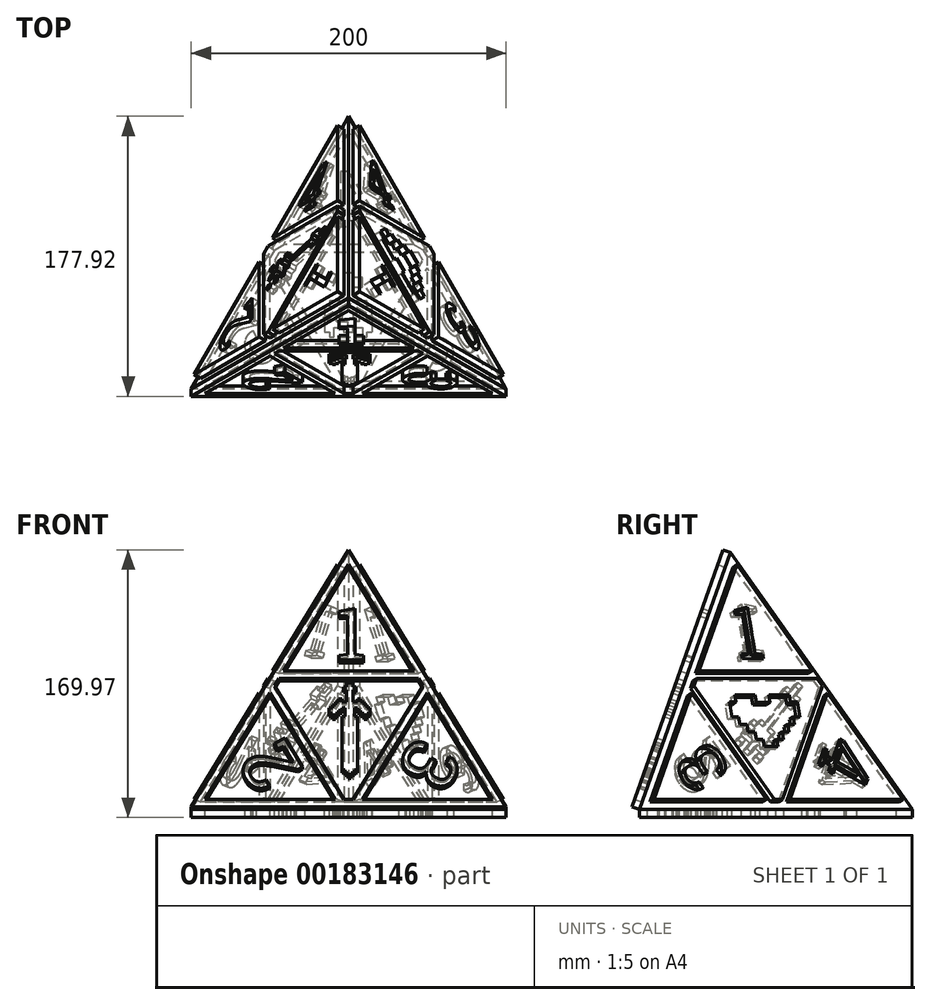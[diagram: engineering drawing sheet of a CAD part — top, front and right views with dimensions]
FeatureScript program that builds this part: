
annotation { "Feature Type Name" : "Feature", "Feature Type Description" : "" }
export const myFeature = defineFeature(function(context is Context, id is Id, definition is map)
    precondition{}
    {
        {
            var Q0;
            Q0=qCreatedBy(makeId("Top.planeOp"),FACE);
            var sketch = newSketch(context, id + "F0", { "sketchPlane" : qUnion([Q0])});
            skLineSegment(sketch, "E0", {"start": v(0, 115.47) * mm, "end": v(100, -57.74) * mm});
            skLineSegment(sketch, "E1", {"start": v(100, -57.74) * mm, "end": v(-100, -57.74) * mm});
            skLineSegment(sketch, "E2", {"start": v(-100, -57.74) * mm, "end": v(0, 115.47) * mm});
            skLineSegment(sketch, "E3", {"start": v(0, 115.47) * mm, "end": v(0, 0) * mm});
            skLineSegment(sketch, "E4", {"start": v(-100, -57.74) * mm, "end": v(0, 0) * mm});
            skLineSegment(sketch, "E5", {"start": v(0, 0) * mm, "end": v(100, -57.74) * mm});
            skPoint(sketch, "E6.orphan", {"position": v(0, -57.74) * mm});
            skLineSegment(sketch, "E7", {"start": v(0, 115.47) * mm, "end": v(0, -57.74) * mm, "construction": true});
            skSolve(sketch);
        }
        {
            assignVariable(context, id + "F1", {"name" : "Angle", "anyValue" : 70.53});
        }
        {
            var Q0;
            Q0=qSketchRegion(id+"F0",true);
            extrude(context, id + "F2", {"entities" : qUnion([Q0]), "depth" : 1000 * mm, "hasDraft" : true, "draftAngle" : (90 - getVariable(context, 'Angle')) * degree, "draftPullDirection" : true});
        }
        {
            var Q0;
            Q0=makeQuery(id+"F2.opExtrude","SWEPT_FACE",FACE,{"disambiguationData":[OSD([sQuery(id+"F0.wireOp",EDGE,"E1")])]});
            var sketch = newSketch(context, id + "F3", { "sketchPlane" : qUnion([Q0])});
            skLineSegment(sketch, "E8", {"start": v(0, 153.96) * mm, "end": v(-100, -19.24) * mm});
            skLineSegment(sketch, "E9", {"start": v(-100, -19.24) * mm, "end": v(100, -19.24) * mm});
            skLineSegment(sketch, "E10", {"start": v(100, -19.24) * mm, "end": v(0, 153.96) * mm});
            skLineSegment(sketch, "E11", {"start": v(-2.89, -14.24) * mm, "end": v(-47.11, 62.36) * mm});
            skLineSegment(sketch, "E12", {"start": v(-44.23, 67.36) * mm, "end": v(44.23, 67.36) * mm});
            skLineSegment(sketch, "E13", {"start": v(47.11, 62.36) * mm, "end": v(2.89, -14.24) * mm});
            skLineSegment(sketch, "E14.0", {"start": v(91.34, -14.24) * mm, "end": v(50, 57.36) * mm});
            skLineSegment(sketch, "E15.0", {"start": v(-41.34, 72.36) * mm, "end": v(41.34, 72.36) * mm});
            skLineSegment(sketch, "E16.0", {"start": v(50, 57.36) * mm, "end": v(8.66, -14.24) * mm});
            skLineSegment(sketch, "E17.trimOffspring", {"start": v(-44.23, 67.36) * mm, "end": v(-47.11, 62.36) * mm});
            skPoint(sketch, "E18.orphan", {"position": v(-50, 67.36) * mm});
            skLineSegment(sketch, "E19.trimOffspring", {"start": v(-50, 57.36) * mm, "end": v(-91.34, -14.24) * mm});
            skLineSegment(sketch, "E20.trimOffspring", {"start": v(41.34, 72.36) * mm, "end": v(0, 143.96) * mm});
            skPoint(sketch, "E21.orphan", {"position": v(50, 67.36) * mm});
            skLineSegment(sketch, "E22.trimOffspring", {"start": v(47.11, 62.36) * mm, "end": v(44.23, 67.36) * mm});
            skLineSegment(sketch, "E23.trimOffspring", {"start": v(-8.66, -14.24) * mm, "end": v(-50, 57.36) * mm});
            skLineSegment(sketch, "E24.trimOffspring", {"start": v(-2.89, -14.24) * mm, "end": v(2.89, -14.24) * mm});
            skLineSegment(sketch, "E25.trimOffspring", {"start": v(8.66, -14.24) * mm, "end": v(91.34, -14.24) * mm});
            skPoint(sketch, "E26.orphan", {"position": v(0, -19.24) * mm});
            skLineSegment(sketch, "E27.trimOffspring", {"start": v(-91.34, -14.24) * mm, "end": v(-8.66, -14.24) * mm});
            skLineSegment(sketch, "E28.trimOffspring", {"start": v(0, 143.96) * mm, "end": v(-41.34, 72.36) * mm});
            skSolve(sketch);
        }
        {
            var Q0;
            Q0=makeQuery(id+"F3.imprint","IMPRINT",FACE,{"disambiguationData":[TD([[makeQuery(id+"F3.imprint","IMPRINT",EDGE,{"derivedFrom":sQuery(id+"F3.wireOp",EDGE,"E8")}),1.0]])]});
            extrude(context, id + "F4", {"entities" : qUnion([Q0]), "operationType" : NewBodyOperationType.ADD, "depth" : 5 * mm});
        }
        {
            var Q0;
            Q0=makeQuery(id+"F4.boolean.opBoolean","SPLIT",FACE,{"disambiguationData":[TD([makeQuery(id+"F4.opExtrude","SWEPT_FACE",FACE,{"disambiguationData":[OSD([sQuery(id+"F3.wireOp",EDGE,"E15.0")])]})])],"derivedFrom":makeQuery(id+"F2.opExtrude","SWEPT_FACE",FACE,{"disambiguationData":[OSD([sQuery(id+"F0.wireOp",EDGE,"E1")])]})});
            var sketch = newSketch(context, id + "F5", { "sketchPlane" : qUnion([Q0])});
            skText(sketch, "E29", { "text": "1", "fontName": "RobotoSlab-Regular.ttf"});
            const initialGuessF5  = {"E29": [-0.00906, 0.07964, 1, 0, 0.03527]};
            skSetInitialGuess(sketch, initialGuessF5);
            skSolve(sketch);
        }
        {
            var Q0;
            Q0=makeQuery(id+"F5.imprint","IMPRINT",FACE,{"disambiguationData":[TD([[makeQuery(id+"F5.imprint","IMPRINT",EDGE,{"derivedFrom":sQuery(id+"F5.wireOp",EDGE,"E29.sketch_text.stroke-0")}),-1.0]])]});
            extrude(context, id + "F6", {"entities" : qUnion([Q0]), "operationType" : NewBodyOperationType.ADD, "depth" : 5 * mm, "hasSecondDirection" : true, "secondDirectionOppositeDirection" : true, "secondDirectionDepth" : 25 * mm});
        }
        {
            var Q0;
            Q0=makeQuery(id+"F4.boolean.opBoolean","SPLIT",FACE,{"disambiguationData":[TD([makeQuery(id+"F4.opExtrude","SWEPT_FACE",FACE,{"disambiguationData":[OSD([sQuery(id+"F3.wireOp",EDGE,"E19.trimOffspring")])]})])],"derivedFrom":makeQuery(id+"F2.opExtrude","SWEPT_FACE",FACE,{"disambiguationData":[OSD([sQuery(id+"F0.wireOp",EDGE,"E1")])]})});
            var sketch = newSketch(context, id + "F7", { "sketchPlane" : qUnion([Q0])});
            skText(sketch, "E30", { "text": "2", "fontName": "RobotoSlab-Regular.ttf"});
            const initialGuessF7  = {"E30": [-0.02807, 0.0057, -0.5, 0.86603, 0.03527]};
            skSetInitialGuess(sketch, initialGuessF7);
            skSolve(sketch);
        }
        {
            var Q0;
            Q0=makeQuery(id+"F7.imprint","IMPRINT",FACE,{"disambiguationData":[TD([[makeQuery(id+"F7.imprint","IMPRINT",EDGE,{"derivedFrom":sQuery(id+"F7.wireOp",EDGE,"E30.sketch_text.stroke-0")}),-1.0]])]});
            extrude(context, id + "F8", {"entities" : qUnion([Q0]), "operationType" : NewBodyOperationType.ADD, "depth" : 5 * mm});
        }
        {
            var Q0;
            Q0=makeQuery(id+"F4.boolean.opBoolean","SPLIT",FACE,{"disambiguationData":[TD([makeQuery(id+"F4.opExtrude","SWEPT_FACE",FACE,{"disambiguationData":[OSD([sQuery(id+"F3.wireOp",EDGE,"E14.0")])]})])],"derivedFrom":makeQuery(id+"F2.opExtrude","SWEPT_FACE",FACE,{"disambiguationData":[OSD([sQuery(id+"F0.wireOp",EDGE,"E1")])]})});
            var sketch = newSketch(context, id + "F9", { "sketchPlane" : qUnion([Q0])});
            skText(sketch, "E31", { "text": "3", "fontName": "RobotoSlab-Regular.ttf"});
            const initialGuessF9  = {"E31": [0.04286, 0.02914, -0.5, -0.86603, 0.03527]};
            skSetInitialGuess(sketch, initialGuessF9);
            skSolve(sketch);
        }
        {
            var Q0;
            Q0=makeQuery(id+"F9.imprint","IMPRINT",FACE,{"disambiguationData":[TD([[makeQuery(id+"F9.imprint","IMPRINT",EDGE,{"derivedFrom":sQuery(id+"F9.wireOp",EDGE,"E31.sketch_text.stroke-0")}),-1.0]])]});
            extrude(context, id + "F10", {"entities" : qUnion([Q0]), "operationType" : NewBodyOperationType.ADD, "depth" : 5 * mm});
        }
        {
            var Q0;
            Q0=makeQuery(id+"F2.opExtrude","SWEPT_FACE",FACE,{"disambiguationData":[OSD([sQuery(id+"F0.wireOp",EDGE,"E0")])]});
            var sketch = newSketch(context, id + "F11", { "sketchPlane" : qUnion([Q0])});
            skLineSegment(sketch, "E32", {"start": v(-29.1, 151.19) * mm, "end": v(101.83, 0) * mm});
            skLineSegment(sketch, "E33", {"start": v(101.83, 0) * mm, "end": v(-94.56, -37.8) * mm});
            skLineSegment(sketch, "E34", {"start": v(-92.67, -32.34) * mm, "end": v(-63.72, 51.24) * mm});
            skLineSegment(sketch, "E35", {"start": v(5.53, -13.44) * mm, "end": v(34.48, 70.14) * mm});
            skLineSegment(sketch, "E36", {"start": v(30.7, 74.5) * mm, "end": v(-56.16, 57.79) * mm});
            skLineSegment(sketch, "E37", {"start": v(-58.05, 52.33) * mm, "end": v(-0.14, -14.53) * mm});
            skLineSegment(sketch, "E38.trimOffspring", {"start": v(-27.2, 141.37) * mm, "end": v(26.92, 78.87) * mm});
            skLineSegment(sketch, "E39.trimOffspring", {"start": v(26.92, 78.87) * mm, "end": v(-54.27, 63.24) * mm});
            skPoint(sketch, "E40.orphan", {"position": v(36.37, 75.6) * mm});
            skLineSegment(sketch, "E41.trimOffspring", {"start": v(92.39, 3.27) * mm, "end": v(11.2, -12.35) * mm});
            skPoint(sketch, "E42.orphan", {"position": v(3.64, -18.9) * mm});
            skLineSegment(sketch, "E43.trimOffspring", {"start": v(11.2, -12.35) * mm, "end": v(38.26, 65.77) * mm});
            skLineSegment(sketch, "E44.trimOffspring", {"start": v(-87, -31.25) * mm, "end": v(-59.94, 46.88) * mm});
            skLineSegment(sketch, "E45.trimOffspring", {"start": v(-92.67, -32.34) * mm, "end": v(-95.5, -32.89) * mm});
            skLineSegment(sketch, "E46.trimOffspring", {"start": v(-59.94, 46.88) * mm, "end": v(-5.81, -15.62) * mm});
            skLineSegment(sketch, "E47.trimOffspring", {"start": v(-61.83, 56.7) * mm, "end": v(-29.1, 151.19) * mm});
            skLineSegment(sketch, "E48.trimOffspring", {"start": v(-58.05, 52.33) * mm, "end": v(-56.16, 57.79) * mm});
            skLineSegment(sketch, "E49.trimOffspring", {"start": v(-54.27, 63.24) * mm, "end": v(-27.2, 141.37) * mm});
            skLineSegment(sketch, "E50.trimOffspring", {"start": v(38.26, 65.77) * mm, "end": v(92.39, 3.27) * mm});
            skLineSegment(sketch, "E51.trimOffspring", {"start": v(30.7, 74.5) * mm, "end": v(34.48, 70.14) * mm});
            skLineSegment(sketch, "E52.trimOffspring", {"start": v(-5.81, -15.62) * mm, "end": v(-87, -31.25) * mm});
            skLineSegment(sketch, "E53.trimOffspring", {"start": v(5.53, -13.44) * mm, "end": v(-0.14, -14.53) * mm});
            skLineSegment(sketch, "E54", {"start": v(-63.72, 51.24) * mm, "end": v(-61.83, 56.7) * mm});
            skSolve(sketch);
        }
        {
            var Q0;
            Q0 = qSketchRegion(id + "F11", true);
            extrude(context, id + "F12", {"entities" : qUnion([Q0]), "operationType" : NewBodyOperationType.ADD, "depth" : 5 * mm});
        }
        {
            var Q0;
            Q0=makeQuery(id+"F2.opExtrude","SWEPT_FACE",FACE,{"disambiguationData":[OSD([sQuery(id+"F0.wireOp",EDGE,"E2")])]});
            var sketch = newSketch(context, id + "F13", { "sketchPlane" : qUnion([Q0])});
            skLineSegment(sketch, "E55", {"start": v(29.1, 151.19) * mm, "end": v(-101.83, 0) * mm});
            skLineSegment(sketch, "E56", {"start": v(-101.83, 0) * mm, "end": v(94.56, -37.8) * mm});
            skLineSegment(sketch, "E57", {"start": v(94.56, -37.8) * mm, "end": v(29.1, 151.19) * mm});
            skLineSegment(sketch, "E58", {"start": v(-5.53, -13.44) * mm, "end": v(-34.48, 70.14) * mm});
            skLineSegment(sketch, "E59", {"start": v(-30.7, 74.5) * mm, "end": v(56.16, 57.79) * mm});
            skLineSegment(sketch, "E60", {"start": v(58.05, 52.33) * mm, "end": v(0.14, -14.53) * mm});
            skLineSegment(sketch, "E61.0", {"start": v(27.2, 141.37) * mm, "end": v(-26.92, 78.87) * mm});
            skLineSegment(sketch, "E62.0", {"start": v(-92.39, 3.27) * mm, "end": v(-11.2, -12.35) * mm});
            skLineSegment(sketch, "E63.0", {"start": v(-26.92, 78.87) * mm, "end": v(54.27, 63.24) * mm});
            skLineSegment(sketch, "E64.trimOffspring", {"start": v(54.27, 63.24) * mm, "end": v(27.2, 141.37) * mm});
            skPoint(sketch, "E65.orphan", {"position": v(61.83, 56.7) * mm});
            skLineSegment(sketch, "E66.trimOffspring", {"start": v(58.05, 52.33) * mm, "end": v(56.16, 57.79) * mm});
            skLineSegment(sketch, "E67.trimOffspring", {"start": v(59.94, 46.88) * mm, "end": v(5.81, -15.62) * mm});
            skLineSegment(sketch, "E68.trimOffspring", {"start": v(87, -31.25) * mm, "end": v(59.94, 46.88) * mm});
            skLineSegment(sketch, "E69.trimOffspring", {"start": v(-11.2, -12.35) * mm, "end": v(-38.26, 65.77) * mm});
            skPoint(sketch, "E70.orphan", {"position": v(-3.64, -18.9) * mm});
            skLineSegment(sketch, "E71.trimOffspring", {"start": v(-5.53, -13.44) * mm, "end": v(0.14, -14.53) * mm});
            skLineSegment(sketch, "E72.trimOffspring", {"start": v(5.81, -15.62) * mm, "end": v(87, -31.25) * mm});
            skLineSegment(sketch, "E73.trimOffspring", {"start": v(-38.26, 65.77) * mm, "end": v(-92.39, 3.27) * mm});
            skLineSegment(sketch, "E74.trimOffspring", {"start": v(-30.7, 74.5) * mm, "end": v(-34.48, 70.14) * mm});
            skPoint(sketch, "E75.orphan", {"position": v(-36.37, 75.6) * mm});
            skSolve(sketch);
        }
        {
            var Q0;
            Q0=makeQuery(id+"F13.imprint","IMPRINT",FACE,{"disambiguationData":[TD([[makeQuery(id+"F13.imprint","IMPRINT",EDGE,{"derivedFrom":sQuery(id+"F13.wireOp",EDGE,"E58")}),-1.0]])]});
            var Q1;
            Q1=makeQuery(id+"F13.imprint","IMPRINT",FACE,{"disambiguationData":[TD([[makeQuery(id+"F13.imprint","IMPRINT",EDGE,{"derivedFrom":sQuery(id+"F13.wireOp",EDGE,"E61.0")}),1.0]])]});
            var Q2;
            Q2=makeQuery(id+"F13.imprint","IMPRINT",FACE,{"disambiguationData":[TD([[makeQuery(id+"F13.imprint","IMPRINT",EDGE,{"derivedFrom":sQuery(id+"F13.wireOp",EDGE,"E62.0")}),1.0]])]});
            var Q3;
            Q3=makeQuery(id+"F13.imprint","IMPRINT",FACE,{"disambiguationData":[TD([[makeQuery(id+"F13.imprint","IMPRINT",EDGE,{"derivedFrom":sQuery(id+"F13.wireOp",EDGE,"E67.trimOffspring")}),1.0]])]});
            extrude(context, id + "F14", {"entities" : qUnion([Q0, Q1, Q2, Q3]), "operationType" : NewBodyOperationType.ADD, "depth" : 5 * mm});
        }
        {
            var Q0;
            Q0=makeQuery(id+"F2.opExtrude","CAP_FACE",FACE,{"disambiguationData":[OSD([sQuery(id+"F0.wireOp",EDGE,"E0"),sQuery(id+"F0.wireOp",EDGE,"E1"),sQuery(id+"F0.wireOp",EDGE,"E2")])],"isStart":true});
            var sketch = newSketch(context, id + "F15", { "sketchPlane" : qUnion([Q0])});
            skLineSegment(sketch, "E76", {"start": v(0, -115.47) * mm, "end": v(-100, 57.74) * mm});
            skLineSegment(sketch, "E77", {"start": v(-100, 57.74) * mm, "end": v(100, 57.74) * mm});
            skLineSegment(sketch, "E78", {"start": v(100, 57.74) * mm, "end": v(0, -115.47) * mm});
            skLineSegment(sketch, "E79", {"start": v(44.23, -28.87) * mm, "end": v(-44.23, -28.87) * mm});
            skLineSegment(sketch, "E80", {"start": v(-47.11, -23.87) * mm, "end": v(-2.89, 52.74) * mm});
            skLineSegment(sketch, "E81", {"start": v(2.89, 52.74) * mm, "end": v(47.11, -23.87) * mm});
            skLineSegment(sketch, "E82.0", {"start": v(41.34, -33.87) * mm, "end": v(-41.34, -33.87) * mm});
            skLineSegment(sketch, "E83.trimOffspring", {"start": v(-44.23, -28.87) * mm, "end": v(-47.11, -23.87) * mm});
            skLineSegment(sketch, "E84.trimOffspring", {"start": v(-50, -18.87) * mm, "end": v(-91.34, 52.74) * mm});
            skLineSegment(sketch, "E85.trimOffspring", {"start": v(-50, -18.87) * mm, "end": v(-8.66, 52.74) * mm});
            skPoint(sketch, "E86.orphan", {"position": v(-50, -28.87) * mm});
            skLineSegment(sketch, "E87.trimOffspring", {"start": v(-91.34, 52.74) * mm, "end": v(-8.66, 52.74) * mm});
            skLineSegment(sketch, "E88.trimOffspring", {"start": v(8.66, 52.74) * mm, "end": v(91.34, 52.74) * mm});
            skPoint(sketch, "E89.orphan", {"position": v(0, 57.74) * mm});
            skLineSegment(sketch, "E90.trimOffspring", {"start": v(8.66, 52.74) * mm, "end": v(50, -18.87) * mm});
            skLineSegment(sketch, "E91.trimOffspring", {"start": v(-2.89, 52.74) * mm, "end": v(2.89, 52.74) * mm});
            skLineSegment(sketch, "E92.trimOffspring", {"start": v(91.34, 52.74) * mm, "end": v(50, -18.87) * mm});
            skPoint(sketch, "E93.orphan", {"position": v(50, -28.87) * mm});
            skLineSegment(sketch, "E94.trimOffspring", {"start": v(41.34, -33.87) * mm, "end": v(0, -105.47) * mm});
            skLineSegment(sketch, "E95.trimOffspring", {"start": v(47.11, -23.87) * mm, "end": v(44.23, -28.87) * mm});
            skLineSegment(sketch, "E96.trimOffspring", {"start": v(0, -105.47) * mm, "end": v(-41.34, -33.87) * mm});
            skSolve(sketch);
        }
        {
            var Q0;
            Q0=makeQuery(id+"F15.imprint","IMPRINT",FACE,{"disambiguationData":[TD([[makeQuery(id+"F15.imprint","IMPRINT",EDGE,{"derivedFrom":sQuery(id+"F15.wireOp",EDGE,"E76")}),1.0]])]});
            extrude(context, id + "F16", {"entities" : qUnion([Q0]), "operationType" : NewBodyOperationType.ADD, "depth" : 5 * mm});
        }
        {
            var Q0;
            Q0=makeQuery(id+"F12.opExtrude","CAP_FACE",FACE,{"disambiguationData":[OSD([sQuery(id+"F11.wireOp",EDGE,"E38.trimOffspring"),sQuery(id+"F11.wireOp",EDGE,"E39.trimOffspring"),sQuery(id+"F11.wireOp",EDGE,"E49.trimOffspring")])],"isStart":false});
            var sketch = newSketch(context, id + "F17", { "sketchPlane" : qUnion([Q0])});
            skText(sketch, "E97", { "text": "1", "fontName": "RobotoSlab-Regular.ttf"});
            const initialGuessF17  = {"E97": [-0.0261, 0.07711, 0.9848, 0.17365, 0.03527]};
            skSetInitialGuess(sketch, initialGuessF17);
            skSolve(sketch);
        }
        {
            var Q0;
            Q0=makeQuery(id+"F17.imprint","IMPRINT",FACE,{"disambiguationData":[TD([[makeQuery(id+"F17.imprint","IMPRINT",EDGE,{"derivedFrom":sQuery(id+"F17.wireOp",EDGE,"E97.sketch_text.stroke-0")}),-1.0]])]});
            extrude(context, id + "F18", {"entities" : qUnion([Q0]), "operationType" : NewBodyOperationType.REMOVE, "oppositeDirection" : true, "depth" : 5 * mm});
        }
        {
            var Q0;
            Q0=makeQuery(id+"F14.opExtrude","CAP_FACE",FACE,{"disambiguationData":[OSD([sQuery(id+"F13.wireOp",EDGE,"E61.0"),sQuery(id+"F13.wireOp",EDGE,"E63.0"),sQuery(id+"F13.wireOp",EDGE,"E64.trimOffspring")])],"isStart":false});
            var sketch = newSketch(context, id + "F19", { "sketchPlane" : qUnion([Q0])});
            skText(sketch, "E98", { "text": "1", "fontName": "RobotoSlab-Regular.ttf"});
            const initialGuessF19  = {"E98": [0.00445, 0.08343, 0.98198, -0.18898, 0.03527]};
            skSetInitialGuess(sketch, initialGuessF19);
            skSolve(sketch);
        }
        {
            var Q0;
            Q0=makeQuery(id+"F19.imprint","IMPRINT",FACE,{"disambiguationData":[TD([[makeQuery(id+"F19.imprint","IMPRINT",EDGE,{"derivedFrom":sQuery(id+"F19.wireOp",EDGE,"E98.sketch_text.stroke-0")}),-1.0]])]});
            extrude(context, id + "F20", {"entities" : qUnion([Q0]), "operationType" : NewBodyOperationType.REMOVE, "oppositeDirection" : true, "depth" : 5 * mm});
        }
        {
            var Q0;
            Q0=makeQuery(id+"F12.opExtrude","CAP_FACE",FACE,{"disambiguationData":[OSD([sQuery(id+"F11.wireOp",EDGE,"E44.trimOffspring"),sQuery(id+"F11.wireOp",EDGE,"E46.trimOffspring"),sQuery(id+"F11.wireOp",EDGE,"E52.trimOffspring")])],"isStart":false});
            var sketch = newSketch(context, id + "F21", { "sketchPlane" : qUnion([Q0])});
            skText(sketch, "E99", { "text": "3", "fontName": "RobotoSlab-Regular.ttf"});
            const initialGuessF21  = {"E99": [-0.03069, -0.00104, -0.65465, 0.75593, 0.03527]};
            skSetInitialGuess(sketch, initialGuessF21);
            skSolve(sketch);
        }
        {
            var Q0;
            Q0=makeQuery(id+"F16.boolean.opBoolean","SPLIT",FACE,{"disambiguationData":[TD([makeQuery(id+"F16.opExtrude","SWEPT_FACE",FACE,{"disambiguationData":[OSD([sQuery(id+"F15.wireOp",EDGE,"E88.trimOffspring")])]})])],"derivedFrom":makeQuery(id+"F2.opExtrude","CAP_FACE",FACE,{"disambiguationData":[OSD([sQuery(id+"F0.wireOp",EDGE,"E0"),sQuery(id+"F0.wireOp",EDGE,"E1"),sQuery(id+"F0.wireOp",EDGE,"E2")])],"isStart":true})});
            var sketch = newSketch(context, id + "F22", { "sketchPlane" : qUnion([Q0])});
            skText(sketch, "E100", { "text": "3", "fontName": "RobotoSlab-Regular.ttf"});
            const initialGuessF22  = {"E100": [0.02773, 0.03386, 0.5, -0.86603, 0.03527]};
            skSetInitialGuess(sketch, initialGuessF22);
            skSolve(sketch);
        }
        {
            var Q0;
            Q0=makeQuery(id+"F22.imprint","IMPRINT",FACE,{"disambiguationData":[TD([[makeQuery(id+"F22.imprint","IMPRINT",EDGE,{"derivedFrom":sQuery(id+"F22.wireOp",EDGE,"E100.sketch_text.stroke-0")}),-1.0]])]});
            extrude(context, id + "F23", {"entities" : qUnion([Q0]), "operationType" : NewBodyOperationType.ADD, "depth" : 5 * mm});
        }
        {
            var Q0;
            Q0 = qSketchRegion(id + "F21", true);
            extrude(context, id + "F24", {"entities" : qUnion([Q0]), "operationType" : NewBodyOperationType.REMOVE, "oppositeDirection" : true, "depth" : 5 * mm});
        }
        {
            var Q0;
            Q0=makeQuery(id+"F16.boolean.opBoolean","SPLIT",FACE,{"disambiguationData":[TD([makeQuery(id+"F16.opExtrude","SWEPT_FACE",FACE,{"disambiguationData":[OSD([sQuery(id+"F15.wireOp",EDGE,"E84.trimOffspring")])]})])],"derivedFrom":makeQuery(id+"F2.opExtrude","CAP_FACE",FACE,{"disambiguationData":[OSD([sQuery(id+"F0.wireOp",EDGE,"E0"),sQuery(id+"F0.wireOp",EDGE,"E1"),sQuery(id+"F0.wireOp",EDGE,"E2")])],"isStart":true})});
            var sketch = newSketch(context, id + "F25", { "sketchPlane" : qUnion([Q0])});
            skText(sketch, "E101", { "text": "2", "fontName": "RobotoSlab-Regular.ttf"});
            const initialGuessF25  = {"E101": [-0.0403, 0.0069, 0.5, 0.86603, 0.03527]};
            skSetInitialGuess(sketch, initialGuessF25);
            skSolve(sketch);
        }
        {
            var Q0;
            Q0=makeQuery(id+"F25.imprint","IMPRINT",FACE,{"disambiguationData":[TD([[makeQuery(id+"F25.imprint","IMPRINT",EDGE,{"derivedFrom":sQuery(id+"F25.wireOp",EDGE,"E101.sketch_text.stroke-0")}),-1.0]])]});
            extrude(context, id + "F26", {"entities" : qUnion([Q0]), "operationType" : NewBodyOperationType.ADD, "depth" : 5 * mm});
        }
        {
            var Q0;
            Q0=makeQuery(id+"F14.opExtrude","CAP_FACE",FACE,{"disambiguationData":[OSD([sQuery(id+"F13.wireOp",EDGE,"E67.trimOffspring"),sQuery(id+"F13.wireOp",EDGE,"E68.trimOffspring"),sQuery(id+"F13.wireOp",EDGE,"E72.trimOffspring")])],"isStart":false});
            var sketch = newSketch(context, id + "F27", { "sketchPlane" : qUnion([Q0])});
            skText(sketch, "E102", { "text": "2", "fontName": "RobotoSlab-Regular.ttf"});
            const initialGuessF27  = {"E102": [0.04802, 0.02153, -0.65465, -0.75593, 0.03527]};
            skSetInitialGuess(sketch, initialGuessF27);
            skSolve(sketch);
        }
        {
            var Q0;
            Q0=makeQuery(id+"F27.imprint","IMPRINT",FACE,{"disambiguationData":[TD([[makeQuery(id+"F27.imprint","IMPRINT",EDGE,{"derivedFrom":sQuery(id+"F27.wireOp",EDGE,"E102.sketch_text.stroke-0")}),-1.0]])]});
            extrude(context, id + "F28", {"entities" : qUnion([Q0]), "operationType" : NewBodyOperationType.REMOVE, "oppositeDirection" : true, "depth" : 5 * mm});
        }
        {
            var Q0;
            Q0=makeQuery(id+"F14.opExtrude","CAP_FACE",FACE,{"disambiguationData":[OSD([sQuery(id+"F13.wireOp",EDGE,"E62.0"),sQuery(id+"F13.wireOp",EDGE,"E69.trimOffspring"),sQuery(id+"F13.wireOp",EDGE,"E73.trimOffspring")])],"isStart":false});
            var sketch = newSketch(context, id + "F29", { "sketchPlane" : qUnion([Q0])});
            skText(sketch, "E103", { "text": "4", "fontName": "RobotoSlab-Regular.ttf"});
            const initialGuessF29  = {"E103": [-0.0261, 0.00665, -0.32732, 0.94491, 0.03527]};
            skSetInitialGuess(sketch, initialGuessF29);
            skSolve(sketch);
        }
        {
            var Q0;
            Q0=makeQuery(id+"F29.imprint","IMPRINT",FACE,{"disambiguationData":[TD([[makeQuery(id+"F29.imprint","IMPRINT",EDGE,{"derivedFrom":sQuery(id+"F29.wireOp",EDGE,"E103.sketch_text.stroke-0")}),-1.0]])]});
            extrude(context, id + "F30", {"entities" : qUnion([Q0]), "operationType" : NewBodyOperationType.REMOVE, "oppositeDirection" : true, "depth" : 5 * mm});
        }
        {
            var Q0;
            Q0=makeQuery(id+"F12.opExtrude","CAP_FACE",FACE,{"disambiguationData":[OSD([sQuery(id+"F11.wireOp",EDGE,"E41.trimOffspring"),sQuery(id+"F11.wireOp",EDGE,"E43.trimOffspring"),sQuery(id+"F11.wireOp",EDGE,"E50.trimOffspring")])],"isStart":false});
            var sketch = newSketch(context, id + "F31", { "sketchPlane" : qUnion([Q0])});
            skText(sketch, "E104", { "text": "4", "fontName": "RobotoSlab-Regular.ttf"});
            const initialGuessF31  = {"E104": [0.03988, 0.04002, -0.32732, -0.94491, 0.03527]};
            skSetInitialGuess(sketch, initialGuessF31);
            skSolve(sketch);
        }
        {
            var Q0;
            Q0=makeQuery(id+"F31.imprint","IMPRINT",FACE,{"disambiguationData":[TD([[makeQuery(id+"F31.imprint","IMPRINT",EDGE,{"derivedFrom":sQuery(id+"F31.wireOp",EDGE,"E104.sketch_text.stroke-0")}),-1.0]])]});
            extrude(context, id + "F32", {"entities" : qUnion([Q0]), "operationType" : NewBodyOperationType.REMOVE, "oppositeDirection" : true, "depth" : 5 * mm});
        }
        {
            var Q0;
            Q0=makeQuery(id+"F16.boolean.opBoolean","SPLIT",FACE,{"disambiguationData":[TD([makeQuery(id+"F16.opExtrude","SWEPT_FACE",FACE,{"disambiguationData":[OSD([sQuery(id+"F15.wireOp",EDGE,"E82.0")])]})])],"derivedFrom":makeQuery(id+"F2.opExtrude","CAP_FACE",FACE,{"disambiguationData":[OSD([sQuery(id+"F0.wireOp",EDGE,"E0"),sQuery(id+"F0.wireOp",EDGE,"E1"),sQuery(id+"F0.wireOp",EDGE,"E2")])],"isStart":true})});
            var sketch = newSketch(context, id + "F33", { "sketchPlane" : qUnion([Q0])});
            skText(sketch, "E105", { "text": "4", "fontName": "RobotoSlab-Regular.ttf"});
            const initialGuessF33  = {"E105": [0.01661, -0.04549, -1, 0, 0.03527]};
            skSetInitialGuess(sketch, initialGuessF33);
            skSolve(sketch);
        }
        {
            var Q0;
            Q0=makeQuery(id+"F33.imprint","IMPRINT",FACE,{"disambiguationData":[TD([[makeQuery(id+"F33.imprint","IMPRINT",EDGE,{"derivedFrom":sQuery(id+"F33.wireOp",EDGE,"E105.sketch_text.stroke-0")}),-1.0]])]});
            extrude(context, id + "F34", {"entities" : qUnion([Q0]), "operationType" : NewBodyOperationType.ADD, "depth" : 5 * mm});
        }
        {
            var Q0;
            Q0=makeQuery(id+"F12.opExtrude","CAP_FACE",FACE,{"disambiguationData":[OSD([sQuery(id+"F11.wireOp",EDGE,"E35"),sQuery(id+"F11.wireOp",EDGE,"E36"),sQuery(id+"F11.wireOp",EDGE,"E37"),sQuery(id+"F11.wireOp",EDGE,"E48.trimOffspring"),sQuery(id+"F11.wireOp",EDGE,"E51.trimOffspring"),sQuery(id+"F11.wireOp",EDGE,"E53.trimOffspring")])],"isStart":false});
            var sketch = newSketch(context, id + "F35", { "sketchPlane" : qUnion([Q0])});
            skLineSegment(sketch, "E106", {"start": v(-12.93, 49.51) * mm, "end": v(-3.11, 51.4) * mm});
            skLineSegment(sketch, "E107", {"start": v(-3.11, 51.4) * mm, "end": v(-4.1, 56.58) * mm});
            skLineSegment(sketch, "E108", {"start": v(-4.1, 56.58) * mm, "end": v(10.62, 59.41) * mm});
            skLineSegment(sketch, "E109", {"start": v(10.62, 59.41) * mm, "end": v(11.57, 54.5) * mm});
            skLineSegment(sketch, "E110", {"start": v(11.57, 54.5) * mm, "end": v(16.48, 55.45) * mm});
            skLineSegment(sketch, "E111", {"start": v(16.48, 55.45) * mm, "end": v(18.37, 45.63) * mm});
            skLineSegment(sketch, "E112", {"start": v(18.37, 45.63) * mm, "end": v(13.46, 44.68) * mm});
            skLineSegment(sketch, "E113", {"start": v(13.46, 44.68) * mm, "end": v(14.4, 39.77) * mm});
            skLineSegment(sketch, "E114", {"start": v(14.4, 39.77) * mm, "end": v(9.5, 38.83) * mm});
            skLineSegment(sketch, "E115", {"start": v(9.5, 38.83) * mm, "end": v(10.44, 33.92) * mm});
            skLineSegment(sketch, "E116", {"start": v(10.44, 33.92) * mm, "end": v(5.53, 32.97) * mm});
            skLineSegment(sketch, "E117", {"start": v(5.53, 32.97) * mm, "end": v(6.47, 28.06) * mm});
            skLineSegment(sketch, "E118", {"start": v(6.47, 28.06) * mm, "end": v(1.56, 27.12) * mm});
            skLineSegment(sketch, "E119", {"start": v(1.56, 27.12) * mm, "end": v(2.5, 22.2) * mm});
            skLineSegment(sketch, "E120", {"start": v(2.5, 22.2) * mm, "end": v(-7.31, 20.32) * mm});
            skLineSegment(sketch, "E121", {"start": v(-25.82, 37.12) * mm, "end": v(-30.73, 36.18) * mm});
            skLineSegment(sketch, "E122", {"start": v(-30.73, 36.18) * mm, "end": v(-32.62, 46) * mm});
            skLineSegment(sketch, "E123", {"start": v(-32.62, 46) * mm, "end": v(-27.71, 46.94) * mm});
            skLineSegment(sketch, "E124", {"start": v(-27.71, 46.94) * mm, "end": v(-28.66, 51.85) * mm});
            skLineSegment(sketch, "E125", {"start": v(-28.66, 51.85) * mm, "end": v(-13.93, 54.69) * mm});
            skLineSegment(sketch, "E126", {"start": v(-13.93, 54.69) * mm, "end": v(-12.93, 49.51) * mm});
            skLineSegment(sketch, "E127", {"start": v(-7.31, 20.32) * mm, "end": v(-8.26, 25.23) * mm});
            skLineSegment(sketch, "E128", {"start": v(-8.26, 25.23) * mm, "end": v(-13.17, 24.28) * mm});
            skLineSegment(sketch, "E129", {"start": v(-13.17, 24.28) * mm, "end": v(-14.11, 29.2) * mm});
            skLineSegment(sketch, "E130", {"start": v(-14.11, 29.2) * mm, "end": v(-19.02, 28.25) * mm});
            skLineSegment(sketch, "E131", {"start": v(-19.02, 28.25) * mm, "end": v(-19.97, 33.16) * mm});
            skLineSegment(sketch, "E132", {"start": v(-19.97, 33.16) * mm, "end": v(-24.88, 32.21) * mm});
            skLineSegment(sketch, "E133", {"start": v(-24.88, 32.21) * mm, "end": v(-25.82, 37.12) * mm});
            skSolve(sketch);
        }
        {
            var Q0;
            Q0=makeQuery(id+"F35.imprint","IMPRINT",FACE,{"disambiguationData":[TD([[makeQuery(id+"F35.imprint","IMPRINT",EDGE,{"derivedFrom":sQuery(id+"F35.wireOp",EDGE,"E106")}),-1.0]])]});
            extrude(context, id + "F36", {"entities" : qUnion([Q0]), "operationType" : NewBodyOperationType.REMOVE, "oppositeDirection" : true, "depth" : 5 * mm});
        }
        {
            var Q0;
            Q0=makeQuery(id+"F14.opExtrude","CAP_FACE",FACE,{"disambiguationData":[OSD([sQuery(id+"F13.wireOp",EDGE,"E58"),sQuery(id+"F13.wireOp",EDGE,"E59"),sQuery(id+"F13.wireOp",EDGE,"E60"),sQuery(id+"F13.wireOp",EDGE,"E66.trimOffspring"),sQuery(id+"F13.wireOp",EDGE,"E71.trimOffspring"),sQuery(id+"F13.wireOp",EDGE,"E74.trimOffspring")])],"isStart":false});
            var sketch = newSketch(context, id + "F37", { "sketchPlane" : qUnion([Q0])});
            skLineSegment(sketch, "E134", {"start": v(-20.05, 66.75) * mm, "end": v(-16.78, 69.05) * mm});
            skLineSegment(sketch, "E135", {"start": v(-16.78, 69.05) * mm, "end": v(-12.19, 62.5) * mm});
            skLineSegment(sketch, "E136", {"start": v(-20.05, 66.75) * mm, "end": v(-15.46, 60.2) * mm});
            skLineSegment(sketch, "E137", {"start": v(-12.19, 62.5) * mm, "end": v(-8.91, 64.79) * mm});
            skLineSegment(sketch, "E138", {"start": v(-8.91, 64.79) * mm, "end": v(-4.32, 58.23) * mm});
            skLineSegment(sketch, "E139", {"start": v(-15.46, 60.2) * mm, "end": v(-18.74, 57.9) * mm});
            skLineSegment(sketch, "E140", {"start": v(-18.74, 57.9) * mm, "end": v(-14.15, 51.35) * mm});
            skLineSegment(sketch, "E141", {"start": v(-14.15, 51.35) * mm, "end": v(-10.88, 53.65) * mm});
            skPoint(sketch, "E141.endSnap0", {"position": v(-16.45, 54.63) * mm});
            skLineSegment(sketch, "E142", {"start": v(-4.32, 58.23) * mm, "end": v(-7.6, 55.94) * mm});
            skLineSegment(sketch, "E143", {"start": v(-10.88, 53.65) * mm, "end": v(7.48, 27.43) * mm});
            skLineSegment(sketch, "E144", {"start": v(-7.6, 55.94) * mm, "end": v(6.23, 36.2) * mm});
            skLineSegment(sketch, "E145", {"start": v(6.17, 36.28) * mm, "end": v(9.44, 38.57) * mm});
            skLineSegment(sketch, "E146", {"start": v(2.9, 33.99) * mm, "end": v(-0.39, 31.7) * mm});
            skLineSegment(sketch, "E147", {"start": v(9.44, 38.57) * mm, "end": v(11.74, 35.3) * mm});
            skLineSegment(sketch, "E148", {"start": v(-0.39, 31.7) * mm, "end": v(1.9, 28.41) * mm});
            skLineSegment(sketch, "E149", {"start": v(1.9, 28.41) * mm, "end": v(-1.37, 26.12) * mm});
            skLineSegment(sketch, "E150", {"start": v(-1.37, 26.12) * mm, "end": v(0.93, 22.84) * mm});
            skLineSegment(sketch, "E151", {"start": v(0.93, 22.84) * mm, "end": v(4.2, 25.14) * mm});
            skLineSegment(sketch, "E152", {"start": v(4.2, 25.14) * mm, "end": v(6.5, 21.86) * mm});
            skLineSegment(sketch, "E153", {"start": v(6.5, 21.86) * mm, "end": v(3.22, 19.57) * mm});
            skLineSegment(sketch, "E154", {"start": v(3.22, 19.57) * mm, "end": v(5.51, 16.3) * mm});
            skLineSegment(sketch, "E155", {"start": v(5.51, 16.3) * mm, "end": v(8.8, 18.58) * mm});
            skLineSegment(sketch, "E156", {"start": v(1.9, 28.41) * mm, "end": v(5.18, 30.7) * mm});
            skLineSegment(sketch, "E157", {"start": v(1.9, 28.41) * mm, "end": v(4.2, 25.14) * mm});
            skLineSegment(sketch, "E158", {"start": v(4.2, 25.14) * mm, "end": v(7.48, 27.43) * mm});
            skLineSegment(sketch, "E159", {"start": v(7.48, 27.43) * mm, "end": v(16.66, 14.33) * mm});
            skLineSegment(sketch, "E160", {"start": v(11.74, 35.3) * mm, "end": v(15.01, 37.6) * mm});
            skLineSegment(sketch, "E161", {"start": v(15.01, 37.6) * mm, "end": v(17.3, 34.32) * mm});
            skLineSegment(sketch, "E162", {"start": v(17.3, 34.32) * mm, "end": v(14.03, 32.02) * mm});
            skLineSegment(sketch, "E163", {"start": v(14.03, 32.02) * mm, "end": v(16.33, 28.74) * mm});
            skLineSegment(sketch, "E164", {"start": v(16.33, 28.74) * mm, "end": v(19.6, 31.04) * mm});
            skLineSegment(sketch, "E165", {"start": v(19.6, 31.04) * mm, "end": v(21.9, 27.76) * mm});
            skLineSegment(sketch, "E166", {"start": v(21.9, 27.76) * mm, "end": v(18.62, 25.47) * mm});
            skLineSegment(sketch, "E167", {"start": v(18.62, 25.47) * mm, "end": v(20.92, 22.2) * mm});
            skLineSegment(sketch, "E168", {"start": v(20.92, 22.2) * mm, "end": v(24.2, 24.49) * mm});
            skLineSegment(sketch, "E169", {"start": v(24.2, 24.49) * mm, "end": v(26.49, 21.2) * mm});
            skLineSegment(sketch, "E170", {"start": v(26.49, 21.2) * mm, "end": v(23.2, 18.91) * mm});
            skLineSegment(sketch, "E171", {"start": v(23.2, 18.91) * mm, "end": v(20.92, 22.2) * mm});
            skLineSegment(sketch, "E172", {"start": v(6.23, 36.2) * mm, "end": v(19.93, 16.62) * mm});
            skLineSegment(sketch, "E173", {"start": v(11.74, 35.3) * mm, "end": v(8.46, 33) * mm});
            skLineSegment(sketch, "E174", {"start": v(14.03, 32.02) * mm, "end": v(10.76, 29.73) * mm});
            skLineSegment(sketch, "E175", {"start": v(16.33, 28.74) * mm, "end": v(18.62, 25.47) * mm});
            skLineSegment(sketch, "E176", {"start": v(20.92, 22.2) * mm, "end": v(17.64, 19.9) * mm});
            skLineSegment(sketch, "E177", {"start": v(16.66, 14.33) * mm, "end": v(19.93, 16.62) * mm});
            skLineSegment(sketch, "E178", {"start": v(6.5, 21.86) * mm, "end": v(8.8, 18.58) * mm});
            skLineSegment(sketch, "E179", {"start": v(8.8, 18.58) * mm, "end": v(12.07, 20.88) * mm});
            skLineSegment(sketch, "E180", {"start": v(6.5, 21.86) * mm, "end": v(9.77, 24.16) * mm});
            skLineSegment(sketch, "E181", {"start": v(16.33, 28.74) * mm, "end": v(13.05, 26.45) * mm});
            skLineSegment(sketch, "E182", {"start": v(18.62, 25.47) * mm, "end": v(15.34, 23.17) * mm});
            skLineSegment(sketch, "E183", {"start": v(11.74, 35.3) * mm, "end": v(14.03, 32.02) * mm});
            skLineSegment(sketch, "E184", {"start": v(8.8, 18.58) * mm, "end": v(11.09, 15.3) * mm});
            skLineSegment(sketch, "E185", {"start": v(11.09, 15.3) * mm, "end": v(14.36, 17.6) * mm});
            skLineSegment(sketch, "E186", {"start": v(11.09, 15.3) * mm, "end": v(7.8, 13.01) * mm});
            skLineSegment(sketch, "E187", {"start": v(7.8, 13.01) * mm, "end": v(10.1, 9.74) * mm});
            skLineSegment(sketch, "E188", {"start": v(10.1, 9.74) * mm, "end": v(13.38, 12.03) * mm});
            skLineSegment(sketch, "E189", {"start": v(13.38, 12.03) * mm, "end": v(11.09, 15.3) * mm});
            skLineSegment(sketch, "E190.0", {"start": v(-16.45, 54.63) * mm, "end": v(-10.88, 53.65) * mm, "construction": true});
            skLineSegment(sketch, "E191", {"start": v(13.38, 12.03) * mm, "end": v(16.66, 14.33) * mm});
            skLineSegment(sketch, "E192", {"start": v(19.93, 16.62) * mm, "end": v(23.2, 18.91) * mm});
            skSolve(sketch);
        }
        {
            var Q0;
            Q0=makeQuery(id+"F37.imprint","IMPRINT",FACE,{"disambiguationData":[TD([[makeQuery(id+"F37.imprint","IMPRINT",EDGE,{"derivedFrom":sQuery(id+"F37.wireOp",EDGE,"E134")}),-1.0]])]});
            var Q1;
            Q1=makeQuery(id+"F37.imprint","IMPRINT",FACE,{"disambiguationData":[TD([[makeQuery(id+"F37.imprint","IMPRINT",EDGE,{"derivedFrom":sQuery(id+"F37.wireOp",EDGE,"E149")}),1.0]])]});
            var Q2;
            Q2=makeQuery(id+"F37.imprint","IMPRINT",FACE,{"disambiguationData":[TD([[makeQuery(id+"F37.imprint","IMPRINT",EDGE,{"derivedFrom":sQuery(id+"F37.wireOp",EDGE,"E153")}),1.0]])]});
            var Q3;
            Q3=makeQuery(id+"F37.imprint","IMPRINT",FACE,{"disambiguationData":[TD([[makeQuery(id+"F37.imprint","IMPRINT",EDGE,{"derivedFrom":sQuery(id+"F37.wireOp",EDGE,"E186")}),1.0]])]});
            var Q4;
            Q4=makeQuery(id+"F37.imprint","IMPRINT",FACE,{"disambiguationData":[TD([[makeQuery(id+"F37.imprint","IMPRINT",EDGE,{"derivedFrom":sQuery(id+"F37.wireOp",EDGE,"E160")}),-1.0]])]});
            var Q5;
            Q5=makeQuery(id+"F37.imprint","IMPRINT",FACE,{"disambiguationData":[TD([[makeQuery(id+"F37.imprint","IMPRINT",EDGE,{"derivedFrom":sQuery(id+"F37.wireOp",EDGE,"E164")}),-1.0]])]});
            var Q6;
            Q6=makeQuery(id+"F37.imprint","IMPRINT",FACE,{"disambiguationData":[TD([[makeQuery(id+"F37.imprint","IMPRINT",EDGE,{"derivedFrom":sQuery(id+"F37.wireOp",EDGE,"E168")}),-1.0]])]});
            var Q7;
            {var subQ0=sQuery(id+"F37.wireOp",EDGE,"E146");Q7=makeQuery(id+"F37.imprint","IMPRINT",FACE,{"disambiguationData":[TD([[makeQuery(id+"F37.imprint","IMPRINT",EDGE,{"derivedFrom":subQ0}),1.0]])]});}
            var Q8;
            {var subQ2=sQuery(id+"F37.wireOp",EDGE,"E156");Q8=makeQuery(id+"F37.imprint","IMPRINT",FACE,{"disambiguationData":[TD([[makeQuery(id+"F37.imprint","IMPRINT",EDGE,{"derivedFrom":subQ2}),-1.0]])]});}
            var Q9;
            Q9=makeQuery(id+"F37.imprint","IMPRINT",FACE,{"disambiguationData":[TD([[makeQuery(id+"F37.imprint","IMPRINT",EDGE,{"derivedFrom":sQuery(id+"F37.wireOp",EDGE,"E152")}),1.0]])]});
            var Q10;
            Q10=makeQuery(id+"F37.imprint","IMPRINT",FACE,{"disambiguationData":[TD([[makeQuery(id+"F37.imprint","IMPRINT",EDGE,{"derivedFrom":sQuery(id+"F37.wireOp",EDGE,"E178")}),1.0]])]});
            var Q11;
            {var subQ4=sQuery(id+"F37.wireOp",EDGE,"E145");Q11=makeQuery(id+"F37.imprint","IMPRINT",FACE,{"disambiguationData":[TD([[makeQuery(id+"F37.imprint","IMPRINT",EDGE,{"derivedFrom":subQ4}),-1.0]])]});}
            var Q12;
            {var subQ0=sQuery(id+"F37.wireOp",EDGE,"E173");Q12=makeQuery(id+"F37.imprint","IMPRINT",FACE,{"disambiguationData":[TD([[makeQuery(id+"F37.imprint","IMPRINT",EDGE,{"derivedFrom":subQ0}),1.0]])]});}
            var Q13;
            Q13=makeQuery(id+"F37.imprint","IMPRINT",FACE,{"disambiguationData":[TD([[makeQuery(id+"F37.imprint","IMPRINT",EDGE,{"derivedFrom":sQuery(id+"F37.wireOp",EDGE,"E163")}),-1.0]])]});
            var Q14;
            Q14=makeQuery(id+"F37.imprint","IMPRINT",FACE,{"disambiguationData":[TD([[makeQuery(id+"F37.imprint","IMPRINT",EDGE,{"derivedFrom":sQuery(id+"F37.wireOp",EDGE,"E175")}),-1.0]])]});
            extrude(context, id + "F38", {"entities" : qUnion([Q0, Q1, Q2, Q3, Q4, Q5, Q6, Q7, Q8, Q9, Q10, Q11, Q12, Q13, Q14]), "operationType" : NewBodyOperationType.REMOVE, "oppositeDirection" : true, "depth" : 5 * mm});
        }
        {
            var Q0;
            Q0=makeQuery(id+"F4.boolean.opBoolean","SPLIT",FACE,{"disambiguationData":[TD([makeQuery(id+"F4.opExtrude","SWEPT_FACE",FACE,{"disambiguationData":[OSD([sQuery(id+"F3.wireOp",EDGE,"E11")])]})])],"derivedFrom":makeQuery(id+"F2.opExtrude","SWEPT_FACE",FACE,{"disambiguationData":[OSD([sQuery(id+"F0.wireOp",EDGE,"E1")])]})});
            var sketch = newSketch(context, id + "F39", { "sketchPlane" : qUnion([Q0])});
            skLineSegment(sketch, "E193", {"start": v(-0.36, 1.57) * mm, "end": v(1.64, 1.57) * mm});
            skLineSegment(sketch, "E194", {"start": v(1.64, 1.57) * mm, "end": v(1.64, 3.57) * mm});
            skLineSegment(sketch, "E195", {"start": v(1.64, 3.57) * mm, "end": v(3.64, 3.57) * mm});
            skLineSegment(sketch, "E196", {"start": v(3.64, 3.57) * mm, "end": v(3.64, 5.57) * mm});
            skLineSegment(sketch, "E197", {"start": v(-0.36, 1.57) * mm, "end": v(-0.36, 3.57) * mm});
            skLineSegment(sketch, "E198", {"start": v(-0.36, 3.57) * mm, "end": v(-2.36, 3.57) * mm});
            skLineSegment(sketch, "E199", {"start": v(-2.36, 3.57) * mm, "end": v(-2.36, 5.57) * mm});
            skLineSegment(sketch, "E200", {"start": v(-2.36, 5.57) * mm, "end": v(-4.36, 5.57) * mm});
            skLineSegment(sketch, "E201", {"start": v(-4.36, 5.57) * mm, "end": v(-4.36, 41.57) * mm});
            skLineSegment(sketch, "E202", {"start": v(3.64, 5.57) * mm, "end": v(5.64, 5.57) * mm});
            skLineSegment(sketch, "E203", {"start": v(5.64, 5.57) * mm, "end": v(5.64, 41.57) * mm});
            skLineSegment(sketch, "E204", {"start": v(-4.36, 41.57) * mm, "end": v(-2.36, 41.57) * mm});
            skLineSegment(sketch, "E205", {"start": v(-2.36, 41.57) * mm, "end": v(-2.36, 47.57) * mm});
            skLineSegment(sketch, "E206", {"start": v(5.64, 41.57) * mm, "end": v(3.64, 41.57) * mm});
            skLineSegment(sketch, "E207", {"start": v(3.64, 41.57) * mm, "end": v(3.64, 47.57) * mm});
            skLineSegment(sketch, "E208", {"start": v(3.64, 47.57) * mm, "end": v(5.64, 47.57) * mm});
            skLineSegment(sketch, "E209", {"start": v(5.64, 47.57) * mm, "end": v(5.64, 45.57) * mm});
            skLineSegment(sketch, "E210", {"start": v(5.64, 45.57) * mm, "end": v(7.64, 45.57) * mm});
            skLineSegment(sketch, "E211", {"start": v(7.64, 45.57) * mm, "end": v(7.64, 43.57) * mm});
            skLineSegment(sketch, "E212", {"start": v(7.64, 43.57) * mm, "end": v(9.64, 43.57) * mm});
            skLineSegment(sketch, "E213", {"start": v(9.64, 43.57) * mm, "end": v(9.64, 41.57) * mm});
            skLineSegment(sketch, "E214", {"start": v(9.64, 41.57) * mm, "end": v(11.64, 41.57) * mm});
            skLineSegment(sketch, "E215", {"start": v(11.64, 41.57) * mm, "end": v(11.64, 43.57) * mm});
            skLineSegment(sketch, "E216", {"start": v(11.64, 43.57) * mm, "end": v(13.64, 43.57) * mm});
            skLineSegment(sketch, "E217", {"start": v(13.64, 43.57) * mm, "end": v(13.64, 47.57) * mm});
            skLineSegment(sketch, "E218", {"start": v(13.64, 47.57) * mm, "end": v(11.64, 47.57) * mm});
            skLineSegment(sketch, "E219", {"start": v(11.64, 47.57) * mm, "end": v(11.64, 49.57) * mm});
            skLineSegment(sketch, "E220", {"start": v(11.64, 49.57) * mm, "end": v(9.64, 49.57) * mm});
            skLineSegment(sketch, "E221", {"start": v(9.64, 49.57) * mm, "end": v(9.64, 51.57) * mm});
            skLineSegment(sketch, "E222", {"start": v(9.64, 51.57) * mm, "end": v(7.64, 51.57) * mm});
            skLineSegment(sketch, "E223", {"start": v(-2.36, 47.57) * mm, "end": v(-4.36, 47.57) * mm});
            skLineSegment(sketch, "E224", {"start": v(-4.36, 47.57) * mm, "end": v(-4.36, 45.57) * mm});
            skLineSegment(sketch, "E225", {"start": v(-4.36, 45.57) * mm, "end": v(-6.36, 45.57) * mm});
            skLineSegment(sketch, "E226", {"start": v(-6.36, 45.57) * mm, "end": v(-6.36, 43.57) * mm});
            skLineSegment(sketch, "E227", {"start": v(-6.36, 43.57) * mm, "end": v(-8.36, 43.57) * mm});
            skLineSegment(sketch, "E228", {"start": v(-8.36, 43.57) * mm, "end": v(-8.36, 41.57) * mm});
            skLineSegment(sketch, "E229", {"start": v(-8.36, 41.57) * mm, "end": v(-10.36, 41.57) * mm});
            skLineSegment(sketch, "E230", {"start": v(-10.36, 41.57) * mm, "end": v(-10.36, 43.57) * mm});
            skLineSegment(sketch, "E231", {"start": v(-10.36, 43.57) * mm, "end": v(-12.36, 43.57) * mm});
            skLineSegment(sketch, "E232", {"start": v(-12.36, 43.57) * mm, "end": v(-12.36, 47.57) * mm});
            skLineSegment(sketch, "E233", {"start": v(-12.36, 47.57) * mm, "end": v(-10.36, 47.57) * mm});
            skLineSegment(sketch, "E234", {"start": v(-10.36, 47.57) * mm, "end": v(-10.36, 49.57) * mm});
            skLineSegment(sketch, "E235", {"start": v(-10.36, 49.57) * mm, "end": v(-8.36, 49.57) * mm});
            skLineSegment(sketch, "E236", {"start": v(-8.36, 49.57) * mm, "end": v(-8.36, 51.57) * mm});
            skLineSegment(sketch, "E237", {"start": v(-8.36, 51.57) * mm, "end": v(-6.36, 51.57) * mm});
            skLineSegment(sketch, "E238", {"start": v(-6.36, 51.57) * mm, "end": v(-6.36, 53.57) * mm});
            skLineSegment(sketch, "E239", {"start": v(-6.36, 53.57) * mm, "end": v(-4.36, 53.57) * mm});
            skLineSegment(sketch, "E240", {"start": v(7.64, 51.57) * mm, "end": v(7.64, 53.57) * mm});
            skLineSegment(sketch, "E241", {"start": v(7.64, 53.57) * mm, "end": v(5.64, 53.57) * mm});
            skLineSegment(sketch, "E242", {"start": v(-4.36, 53.57) * mm, "end": v(-4.36, 51.57) * mm});
            skLineSegment(sketch, "E243", {"start": v(-4.36, 51.57) * mm, "end": v(-1.36, 51.57) * mm});
            skLineSegment(sketch, "E244", {"start": v(-1.36, 51.57) * mm, "end": v(-1.36, 59.57) * mm});
            skLineSegment(sketch, "E245", {"start": v(5.64, 53.57) * mm, "end": v(5.64, 51.57) * mm});
            skLineSegment(sketch, "E246", {"start": v(5.64, 51.57) * mm, "end": v(2.64, 51.57) * mm});
            skLineSegment(sketch, "E247", {"start": v(2.64, 51.57) * mm, "end": v(2.64, 59.57) * mm});
            skLineSegment(sketch, "E248", {"start": v(-1.36, 59.57) * mm, "end": v(-3.36, 59.57) * mm});
            skLineSegment(sketch, "E249", {"start": v(-3.36, 59.57) * mm, "end": v(-3.36, 61.57) * mm});
            skLineSegment(sketch, "E250", {"start": v(4.64, 61.57) * mm, "end": v(4.64, 59.57) * mm});
            skLineSegment(sketch, "E251", {"start": v(4.64, 59.57) * mm, "end": v(2.64, 59.57) * mm});
            skLineSegment(sketch, "E252", {"start": v(-3.36, 61.57) * mm, "end": v(-1.36, 61.57) * mm});
            skLineSegment(sketch, "E253", {"start": v(-1.36, 61.57) * mm, "end": v(-1.36, 64.3) * mm});
            skLineSegment(sketch, "E254", {"start": v(-1.36, 64.3) * mm, "end": v(2.64, 64.3) * mm});
            skLineSegment(sketch, "E255", {"start": v(2.64, 64.3) * mm, "end": v(2.64, 61.57) * mm});
            skLineSegment(sketch, "E256", {"start": v(2.64, 61.57) * mm, "end": v(4.64, 61.57) * mm});
            skSolve(sketch);
        }
        {
            var Q0;
            Q0=makeQuery(id+"F39.imprint","IMPRINT",FACE,{"disambiguationData":[TD([[makeQuery(id+"F39.imprint","IMPRINT",EDGE,{"derivedFrom":sQuery(id+"F39.wireOp",EDGE,"E193")}),1.0]])]});
            extrude(context, id + "F40", {"entities" : qUnion([Q0]), "operationType" : NewBodyOperationType.ADD, "depth" : 5 * mm});
        }
        {
            var Q0;
            Q0=makeQuery(id+"F16.boolean.opBoolean","SPLIT",FACE,{"disambiguationData":[TD([makeQuery(id+"F16.opExtrude","SWEPT_FACE",FACE,{"disambiguationData":[OSD([sQuery(id+"F15.wireOp",EDGE,"E79")])]})])],"derivedFrom":makeQuery(id+"F2.opExtrude","CAP_FACE",FACE,{"disambiguationData":[OSD([sQuery(id+"F0.wireOp",EDGE,"E0"),sQuery(id+"F0.wireOp",EDGE,"E1"),sQuery(id+"F0.wireOp",EDGE,"E2")])],"isStart":true})});
            var sketch = newSketch(context, id + "F41", { "sketchPlane" : qUnion([Q0])});
            skLineSegment(sketch, "E257", {"start": v(14.72, 14.03) * mm, "end": v(11.72, 14.03) * mm});
            skLineSegment(sketch, "E258", {"start": v(11.72, 14.03) * mm, "end": v(11.72, 11.03) * mm});
            skLineSegment(sketch, "E259", {"start": v(11.72, 11.03) * mm, "end": v(14.72, 11.03) * mm});
            skLineSegment(sketch, "E260", {"start": v(14.72, 11.03) * mm, "end": v(14.72, 5.03) * mm});
            skLineSegment(sketch, "E261", {"start": v(14.72, 5.03) * mm, "end": v(11.72, 5.03) * mm});
            skLineSegment(sketch, "E262", {"start": v(11.72, 5.03) * mm, "end": v(11.72, 2.03) * mm});
            skLineSegment(sketch, "E263", {"start": v(11.72, 2.03) * mm, "end": v(5.72, 2.03) * mm});
            skLineSegment(sketch, "E264", {"start": v(5.72, 2.03) * mm, "end": v(5.72, -0.97) * mm});
            skLineSegment(sketch, "E265", {"start": v(5.72, -0.97) * mm, "end": v(2.72, -0.97) * mm});
            skLineSegment(sketch, "E266", {"start": v(2.72, -0.97) * mm, "end": v(2.72, -6.97) * mm});
            skLineSegment(sketch, "E267", {"start": v(2.72, -6.97) * mm, "end": v(8.72, -6.97) * mm});
            skLineSegment(sketch, "E268", {"start": v(8.72, -6.97) * mm, "end": v(8.72, -12.97) * mm});
            skLineSegment(sketch, "E269", {"start": v(8.72, -12.97) * mm, "end": v(2.72, -12.97) * mm});
            skLineSegment(sketch, "E270", {"start": v(2.72, -12.97) * mm, "end": v(2.72, -15.97) * mm});
            skLineSegment(sketch, "E271", {"start": v(2.72, -15.97) * mm, "end": v(-3.28, -15.97) * mm});
            skLineSegment(sketch, "E272", {"start": v(-3.28, -15.97) * mm, "end": v(-3.28, -0.97) * mm});
            skLineSegment(sketch, "E273", {"start": v(-3.28, -0.97) * mm, "end": v(-6.28, -0.97) * mm});
            skLineSegment(sketch, "E274", {"start": v(-6.28, -0.97) * mm, "end": v(-6.28, 2.03) * mm});
            skLineSegment(sketch, "E275", {"start": v(-6.28, 2.03) * mm, "end": v(-12.28, 2.03) * mm});
            skLineSegment(sketch, "E276", {"start": v(-12.28, 2.03) * mm, "end": v(-12.28, 5.03) * mm});
            skLineSegment(sketch, "E277", {"start": v(-12.28, 5.03) * mm, "end": v(-15.28, 5.03) * mm});
            skLineSegment(sketch, "E278", {"start": v(-15.28, 5.03) * mm, "end": v(-15.28, 11.03) * mm});
            skLineSegment(sketch, "E279", {"start": v(-15.28, 11.03) * mm, "end": v(-12.28, 11.03) * mm});
            skLineSegment(sketch, "E280", {"start": v(-12.28, 11.03) * mm, "end": v(-12.28, 14.03) * mm});
            skLineSegment(sketch, "E281", {"start": v(-12.28, 14.03) * mm, "end": v(-15.28, 14.03) * mm});
            skLineSegment(sketch, "E282", {"start": v(-15.28, 18.75) * mm, "end": v(-15.28, 21.75) * mm});
            skLineSegment(sketch, "E283", {"start": v(-15.28, 21.75) * mm, "end": v(-12.28, 21.75) * mm});
            skLineSegment(sketch, "E284", {"start": v(-12.28, 21.75) * mm, "end": v(-12.28, 24.75) * mm});
            skLineSegment(sketch, "E285", {"start": v(-12.28, 24.75) * mm, "end": v(-9.28, 24.75) * mm});
            skLineSegment(sketch, "E286", {"start": v(-9.28, 24.75) * mm, "end": v(-9.28, 21.75) * mm});
            skLineSegment(sketch, "E287", {"start": v(-9.28, 21.75) * mm, "end": v(-9.28, 18.75) * mm});
            skLineSegment(sketch, "E288", {"start": v(-9.28, 18.75) * mm, "end": v(-3.28, 18.75) * mm});
            skLineSegment(sketch, "E289", {"start": v(-3.28, 18.75) * mm, "end": v(-3.28, 21.75) * mm});
            skLineSegment(sketch, "E290", {"start": v(-3.28, 21.75) * mm, "end": v(2.72, 21.75) * mm});
            skLineSegment(sketch, "E291", {"start": v(2.72, 21.75) * mm, "end": v(2.72, 18.75) * mm});
            skLineSegment(sketch, "E292", {"start": v(2.72, 18.75) * mm, "end": v(8.72, 18.75) * mm});
            skLineSegment(sketch, "E293", {"start": v(8.72, 18.75) * mm, "end": v(8.72, 24.75) * mm});
            skLineSegment(sketch, "E294", {"start": v(8.72, 24.75) * mm, "end": v(11.72, 24.75) * mm});
            skLineSegment(sketch, "E295", {"start": v(11.72, 24.75) * mm, "end": v(11.72, 21.75) * mm});
            skLineSegment(sketch, "E296", {"start": v(11.72, 21.75) * mm, "end": v(14.72, 21.75) * mm});
            skLineSegment(sketch, "E297", {"start": v(14.72, 18.75) * mm, "end": v(14.72, 21.75) * mm});
            skLineSegment(sketch, "E298", {"start": v(-15.28, 18.75) * mm, "end": v(-15.28, 14.03) * mm});
            skLineSegment(sketch, "E299", {"start": v(14.72, 14.03) * mm, "end": v(14.72, 18.75) * mm});
            skSolve(sketch);
        }
        {
            var Q0;
            Q0=makeQuery(id+"F41.imprint","IMPRINT",FACE,{"disambiguationData":[TD([[makeQuery(id+"F41.imprint","IMPRINT",EDGE,{"derivedFrom":sQuery(id+"F41.wireOp",EDGE,"E257")}),-1.0]])]});
            extrude(context, id + "F42", {"entities" : qUnion([Q0]), "operationType" : NewBodyOperationType.ADD, "depth" : 5 * mm});
        }
        {
            var Q0;
            Q0=makeQuery(id+"F42.opExtrude","CAP_FACE",FACE,{"disambiguationData":[OSD([sQuery(id+"F41.wireOp",EDGE,"E257"),sQuery(id+"F41.wireOp",EDGE,"E258"),sQuery(id+"F41.wireOp",EDGE,"E259"),sQuery(id+"F41.wireOp",EDGE,"E260"),sQuery(id+"F41.wireOp",EDGE,"E261"),sQuery(id+"F41.wireOp",EDGE,"E262"),sQuery(id+"F41.wireOp",EDGE,"E263"),sQuery(id+"F41.wireOp",EDGE,"E264"),sQuery(id+"F41.wireOp",EDGE,"E265"),sQuery(id+"F41.wireOp",EDGE,"E266"),sQuery(id+"F41.wireOp",EDGE,"E267"),sQuery(id+"F41.wireOp",EDGE,"E268"),sQuery(id+"F41.wireOp",EDGE,"E269"),sQuery(id+"F41.wireOp",EDGE,"E270"),sQuery(id+"F41.wireOp",EDGE,"E271"),sQuery(id+"F41.wireOp",EDGE,"E272"),sQuery(id+"F41.wireOp",EDGE,"E273"),sQuery(id+"F41.wireOp",EDGE,"E274"),sQuery(id+"F41.wireOp",EDGE,"E275"),sQuery(id+"F41.wireOp",EDGE,"E276"),sQuery(id+"F41.wireOp",EDGE,"E277"),sQuery(id+"F41.wireOp",EDGE,"E278"),sQuery(id+"F41.wireOp",EDGE,"E279"),sQuery(id+"F41.wireOp",EDGE,"E280"),sQuery(id+"F41.wireOp",EDGE,"E281"),sQuery(id+"F41.wireOp",EDGE,"E282"),sQuery(id+"F41.wireOp",EDGE,"E283"),sQuery(id+"F41.wireOp",EDGE,"E284"),sQuery(id+"F41.wireOp",EDGE,"E285"),sQuery(id+"F41.wireOp",EDGE,"E286"),sQuery(id+"F41.wireOp",EDGE,"E287"),sQuery(id+"F41.wireOp",EDGE,"E288"),sQuery(id+"F41.wireOp",EDGE,"E289"),sQuery(id+"F41.wireOp",EDGE,"E290"),sQuery(id+"F41.wireOp",EDGE,"E291"),sQuery(id+"F41.wireOp",EDGE,"E292"),sQuery(id+"F41.wireOp",EDGE,"E293"),sQuery(id+"F41.wireOp",EDGE,"E294"),sQuery(id+"F41.wireOp",EDGE,"E295"),sQuery(id+"F41.wireOp",EDGE,"E296"),sQuery(id+"F41.wireOp",EDGE,"E297"),sQuery(id+"F41.wireOp",EDGE,"E298"),sQuery(id+"F41.wireOp",EDGE,"E299")])],"isStart":false});
            var sketch = newSketch(context, id + "F43", { "sketchPlane" : qUnion([Q0])});
            skLineSegment(sketch, "E300", {"start": v(-7.83, 14.91) * mm, "end": v(-5.83, 14.91) * mm});
            skLineSegment(sketch, "E301", {"start": v(-5.83, 14.91) * mm, "end": v(-5.83, 12.91) * mm});
            skLineSegment(sketch, "E302", {"start": v(-7.83, 14.91) * mm, "end": v(-7.83, 10.91) * mm});
            skLineSegment(sketch, "E303", {"start": v(-7.83, 10.91) * mm, "end": v(-5.83, 10.91) * mm});
            skLineSegment(sketch, "E304", {"start": v(-5.83, 12.91) * mm, "end": v(-3.83, 12.91) * mm});
            skLineSegment(sketch, "E305", {"start": v(2.97, 13.11) * mm, "end": v(2.97, 9.11) * mm});
            skLineSegment(sketch, "E306", {"start": v(-3.83, 8.91) * mm, "end": v(-5.83, 8.91) * mm});
            skLineSegment(sketch, "E307", {"start": v(-5.83, 8.91) * mm, "end": v(-5.83, 10.91) * mm});
            skLineSegment(sketch, "E308.MirrorCS", {"start": v(6.97, 11.11) * mm, "end": v(4.97, 11.11) * mm});
            skLineSegment(sketch, "E309.MirrorCS", {"start": v(4.97, 15.11) * mm, "end": v(4.97, 13.11) * mm});
            skLineSegment(sketch, "E310.MirrorCS", {"start": v(4.97, 13.11) * mm, "end": v(2.97, 13.11) * mm});
            skLineSegment(sketch, "E311.MirrorCS", {"start": v(6.97, 15.11) * mm, "end": v(6.97, 11.11) * mm});
            skLineSegment(sketch, "E312.MirrorCS", {"start": v(6.97, 15.11) * mm, "end": v(4.97, 15.11) * mm});
            skLineSegment(sketch, "E313.MirrorCS", {"start": v(4.97, 9.11) * mm, "end": v(4.97, 11.11) * mm});
            skLineSegment(sketch, "E314.MirrorCS", {"start": v(2.97, 9.11) * mm, "end": v(4.97, 9.11) * mm});
            skLineSegment(sketch, "E315", {"start": v(-3.83, 12.91) * mm, "end": v(-3.83, 8.91) * mm});
            skSolve(sketch);
        }
        {
            var Q0;
            Q0=makeQuery(id+"F43.imprint","IMPRINT",FACE,{"disambiguationData":[TD([[makeQuery(id+"F43.imprint","IMPRINT",EDGE,{"derivedFrom":sQuery(id+"F43.wireOp",EDGE,"E300")}),-1.0]])]});
            var Q1;
            Q1=makeQuery(id+"F43.imprint","IMPRINT",FACE,{"disambiguationData":[TD([[makeQuery(id+"F43.imprint","IMPRINT",EDGE,{"derivedFrom":sQuery(id+"F43.wireOp",EDGE,"E305")}),1.0]])]});
            extrude(context, id + "F44", {"entities" : qUnion([Q0, Q1]), "operationType" : NewBodyOperationType.REMOVE, "oppositeDirection" : true, "depth" : 5 * mm});
        }
    });
